# Revit family: Showerhead-American_Standard-Spectra-9038074_Series
name_source: partatom
category: Plumbing Fixtures
units: mm (PartAtom-declared; Revit-internal decimal feet)

## family parameters
Always vertical = No
Cut with Voids When Loaded = No
OmniClass Number = 23.45.05.14.17
OmniClass Title = Showers
Part Type = Normal
Room Calculation Point = No
Round Connector Dimension = Use Diameter
Shared = Yes
Work Plane-Based = Yes

## types (5) — shared parameters
Assembly Code = D2010710
CW Connection = No
CWFU = 3
Default Elevation = 0"
Description = Spectra Fixed™ 7-Inch 1.8 gpm/6.8 L/min Fixed Showerhead
Flow Rate = 1.8 gpm/ 6.8 L/min.
HW Connection = No
HWFU = 3
Height = 3 3/16"
Installation Type = Wall Mounted
Length = 7 3/16"
Manufacturer = American Standard
Price = Prices may vary. Please consult Manufacturer Representative for most up-to-date price list.
Product Documentation Link = https://americanstandard.box.com
Product Page URL = https://www.americanstandard-us.com
Revised Date = 11/18/2022
Tempered Water Connection = Yes
Tempered Water Connection Diameter = 1/2"
Tempered Water Connection Radius = 1/4"
URL = https://www.americanstandard-us.com
Vent Connection = No
WFU = 4
Warranty Information = One Year General Product Warranty
Waste Connection = No
Width = 1 3/8"

## per-type parameters (varying)
| type | Finish | Material |
| 9038074.002 | Brass-American Standard-002-Polished Chrome | Brass-American Standard-002-Polished Chrome |
| 9038074.243 | Brass-American Standard-243-Matte Black | Brass-American Standard-243-Matte Black |
| 9038074.278 | Brass-American Standard-278-Legacy Bronze | Brass-American Standard-278-Legacy Bronze |
| 9038074.295 | Brass-American Standard-295-Brushed Nickel | Brass-American Standard-295-Brushed Nickel |
| 9038074.013 | Brass-American Standard-013-Polished Nickel | Brass-American Standard-013-Polished Nickel |

note: column(s) folded — value = type name in every type: Model

## geometry (parser evidence)
native form markers: Sweep x2
no freeform markers — native parametric forms only
